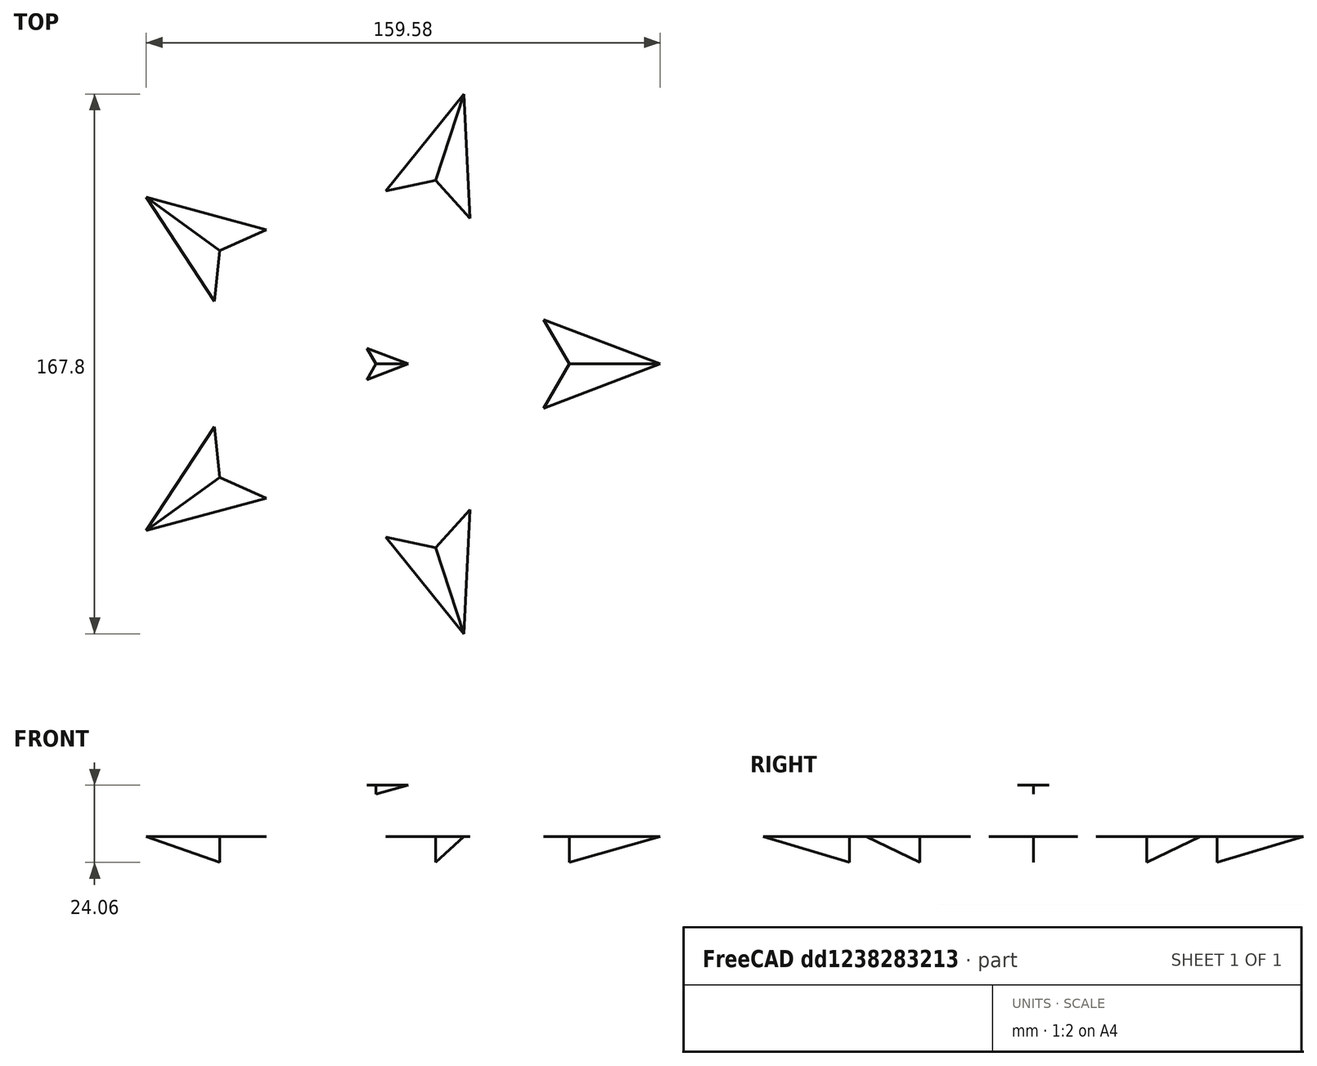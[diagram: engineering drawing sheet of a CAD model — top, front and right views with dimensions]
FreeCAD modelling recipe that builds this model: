
FCSTD DOCUMENT  (FreeCAD 1.1R38827 (Git))
Label: composit_stand3_basement_bearing_holder_main
License: All rights reserved
LicenseURL: http://en.wikipedia.org/wiki/All_rights_reserved
objects: Part::FeaturePython×3, Sketcher::SketchObject×1
note: 5 computed .brp shape members not serialized (recipe doc carries the construction recipe); baked Part::Feature solids carry a one-line shape summary decoded from their .brp
EXTERNAL_REF file=../bearing_d100.FCStd obj=Sketch

FEATURE [Sketcher::SketchObject] Sketch
  ArcFitTolerance = 0
  FullyConstrained = true
  MakeInternals = false
  expr: .Constraints.d = <<bearing_d100>>#<<main_Sketch>>.Constraints.max_r * 2 + 40 mm
  sketch-geometry (1):
    g0: Circle CenterX=0 CenterY=0 CenterZ=0 NormalX=0 NormalY=0 NormalZ=1 AngleXU=0 Radius=70
  constraints (2):
    c: Coincident(g0,g-1)
    c: Diameter(g0) = 140  'd'
FEATURE [Part::FeaturePython] PolarArray  # WARN: FeaturePython — macro-defined, semantics opaque (R4)
  Alignment = 0
  AttacherType = Attacher::AttachEngine3D
  CellStart = A1
  Count = 5
  DistributionLaw = 0
  EndInclusive = false
  ExposePlacement = false
  FlipX = false
  FlipZ = false
  GeneratorMode = 0
  MarkerShape = 1
  MarkerSize = 0
  NumElements = 5
  OrientMode = 2
  Radius = 60
  Reverse = false
  SpanEnd = 360
  SpanStart = 0
  Step = 72
  Type = lattice2PolarArray2.PolarArray
  UseArcRadius = false
  UseArcRange = 0
  VSGVersion = 1
  Values = 0.0 | 72.0 | 144.0 | 216.0 | 288.0
  ValuesSource = 2
  isLattice = 1
  expr: Radius = <<bearing_d100>>#<<main_Sketch>>.Constraints.max_r + 10 mm
FEATURE [Part::FeaturePython] Join  label="holes_placements"  # WARN: FeaturePython — macro-defined, semantics opaque (R4)
  ExposePlacement = false
  Interleave = false
  Links = -> [PolarArray]
  MarkerShape = 1
  MarkerSize = 0
  NumElements = 5
  Type = lattice2JoinArrays.JoinArrays
  isLattice = 1
FEATURE [Part::FeaturePython] Placment  label="bearing_placement"  # WARN: FeaturePython — macro-defined, semantics opaque (R4)
  AttacherType = Attacher::AttachEngine3D
  ExposePlacement = true
  MarkerShape = 1
  MarkerSize = 10
  NumElements = 1
  Placement = pos=(0,0,16) rot=(0,0,1;0rad)
  Type = lattice2AttachablePlacement.AttachablePlacement
  isLattice = 1
